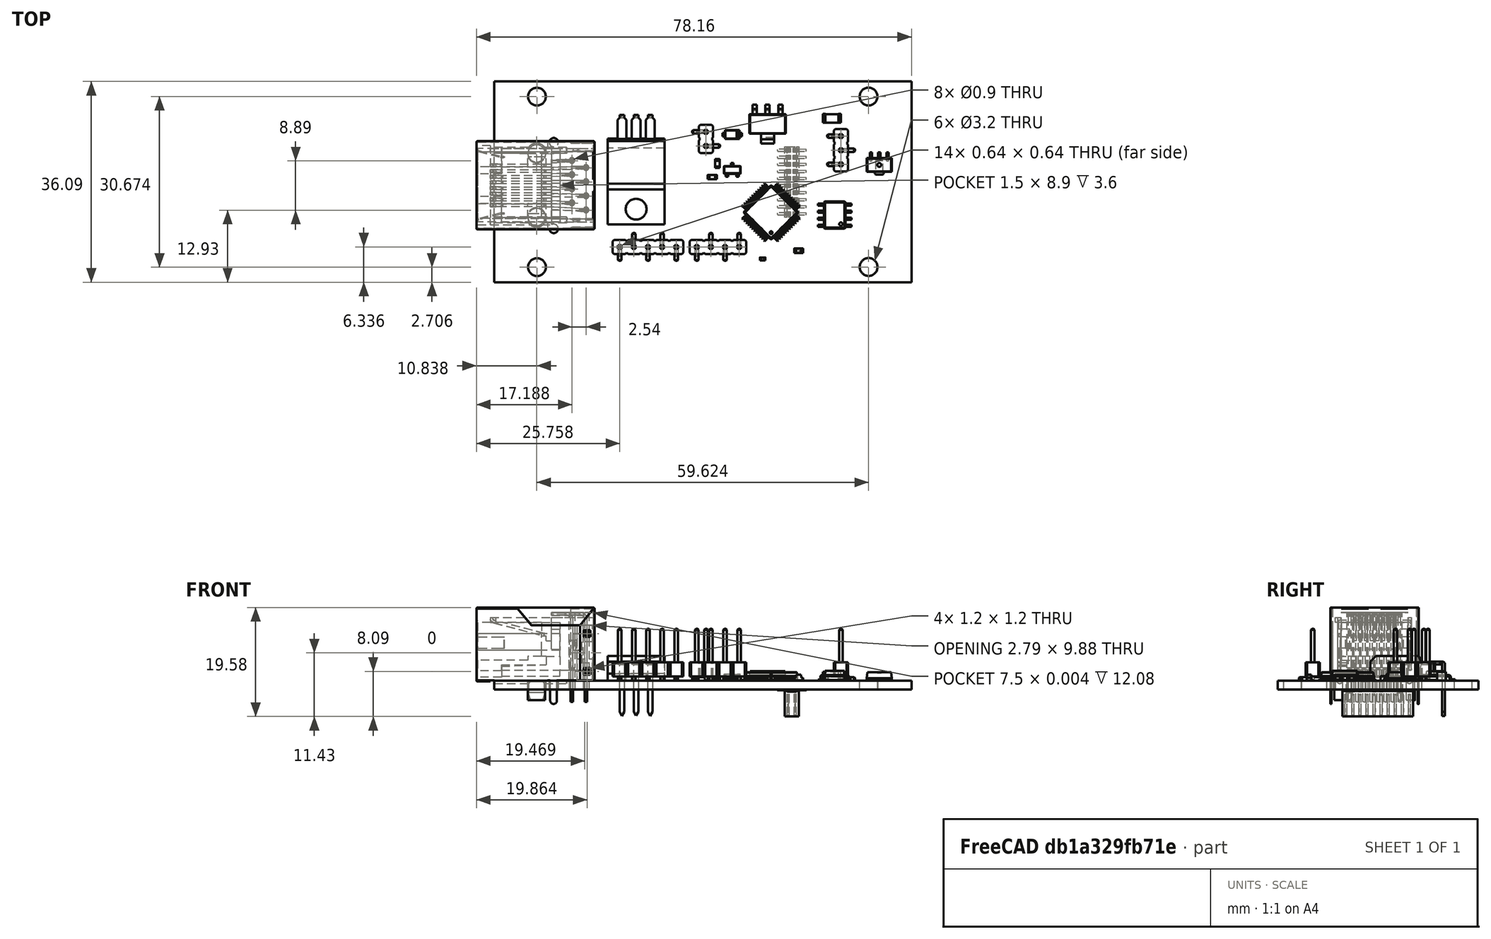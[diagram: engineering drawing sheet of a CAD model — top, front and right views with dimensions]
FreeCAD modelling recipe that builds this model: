
FCSTD DOCUMENT  (FreeCAD 0.19R24276 (Git))
Label: controle
License: Creative Commons Attribution-NonCommercial-ShareAlike
LicenseURL: http://creativecommons.org/licenses/by-nc-sa/4.0/
objects: App::Link×24, Part::Feature×19, App::LinkGroup×8, PartDesign::Line×4, PartDesign::CoordinateSystem×2, Sketcher::SketchObject×1, App::Part×1
note: 26 computed .brp shape members not serialized (recipe doc carries the construction recipe); baked Part::Feature solids carry a one-line shape summary decoded from their .brp

FEATURE [PartDesign::CoordinateSystem] Local_CS_266e
  AttacherType = Attacher::AttachEngine3D
FEATURE [Part::Feature] Pcb_266e
  Placement = pos=(-125.663,89.27,0) rot=(0,0,1;0rad)
  shape: bbox 75 x 36.09 x 1.6 mm, 22 faces (baked)
FEATURE [Sketcher::SketchObject] PCB_Sketch_266e
  FullyConstrained = false
  sketch-geometry (4):
    g0: LineSegment StartX=70.0635 StartY=0.77064 StartZ=0 EndX=-4.94 EndY=0.77 EndZ=0
    g1: LineSegment StartX=70.0635 StartY=36.856 StartZ=0 EndX=70.0635 EndY=0.77064 EndZ=0
    g2: LineSegment StartX=-4.94 StartY=36.856 StartZ=0 EndX=70.0635 EndY=36.856 EndZ=0
    g3: LineSegment StartX=-4.94 StartY=0.77 StartZ=0 EndX=-4.94 EndY=36.856 EndZ=0
  constraints (4):
    c: Coincident(g0,g3)
    c: Coincident(g2,g3)
    c: Coincident(g0,g1)
    c: Coincident(g1,g2)
FEATURE [App::LinkGroup] Board_Geoms_266e
  ElementList = -> [Pcb_266e,Local_CS_266e,PCB_Sketch_266e]
  LinkMode = 0
FEATURE [App::LinkGroup] TopV_266e
  LinkMode = 0
FEATURE [App::LinkGroup] BotV_266e
  LinkMode = 0
FEATURE [App::LinkGroup] Step_Virtual_Models_266e
  ElementList = -> [TopV_266e,BotV_266e]
  LinkMode = 0
FEATURE [Part::Feature] Shape  label="R103_R_0603_1608Metric_607532D5"
  Placement = pos=(35.1841,22.092,0) rot=(0,0,-1;1.5708rad)
  shape: bbox 0.8 x 1.6 x 0.45 mm, 26 faces (baked)
FEATURE [Part::Feature] Shape001  label="J103_PinHeader_1x02_P254mm_Vertical_SMD_Pin1Left_60752E1C"
  Placement = pos=(33.1521,26.537,0) rot=(0,0,1;0rad)
  shape: bbox 5 x 5.08 x 9.3 mm, 58 faces (baked)
FEATURE [App::Link] R103_R_0603_1608Metric_607532D5_ln_  label="R102_R_0603_1608Metric_60753017"
  LinkPlacement = pos=(38.8671,17.266,0) rot=(0,0,1;3.14159rad)
  LinkedObject = -> Shape
  Placement = pos=(38.8671,17.266,0) rot=(0,0,1;3.14159rad)
FEATURE [App::Link] R103_R_0603_1608Metric_607532D5_ln_001  label="R101_R_0603_1608Metric_60753692"
  LinkPlacement = pos=(37.9781,24.505,0) rot=(0,0,1;3.14159rad)
  LinkedObject = -> Shape
  Placement = pos=(37.9781,24.505,0) rot=(0,0,1;3.14159rad)
FEATURE [Part::Feature] Shape002  label="Q101_SOT_23_6075318C"
  Placement = pos=(37.8511,20.949,0) rot=(0,0,1;1.5708rad)
  shape: bbox 3 x 2.5 x 1.2 mm, 76 faces (baked)
FEATURE [Part::Feature] Shape003  label="C104_C_1206_3216Metric_60753A85"
  Placement = pos=(55.7581,30.22,0) rot=(0,0,1;3.14159rad)
  shape: bbox 3.2 x 1.6 x 1.6 mm, 28 faces (baked)
FEATURE [App::Link] C104_C_1206_3216Metric_60753A85_ln_  label="C103_C_1206_3216Metric_60752CED"
  LinkPlacement = pos=(40.8991,21.838,0) rot=(0,0,1;1.5708rad)
  LinkedObject = -> Shape003
  Placement = pos=(40.8991,21.838,0) rot=(0,0,1;1.5708rad)
FEATURE [App::Link] C104_C_1206_3216Metric_60753A85_ln_001  label="C102_C_1206_3216Metric_60752EF7"
  LinkPlacement = pos=(43.3121,21.838,0) rot=(0,0,1;1.5708rad)
  LinkedObject = -> Shape003
  Placement = pos=(43.3121,21.838,0) rot=(0,0,1;1.5708rad)
FEATURE [App::Link] C104_C_1206_3216Metric_60753A85_ln_002  label="C12_C_1206_3216Metric_60752D4D"
  LinkPlacement = pos=(57.7393,7.25838,0) rot=(0,0,1;3.14159rad)
  LinkedObject = -> Shape003
  Placement = pos=(57.7393,7.25838,0) rot=(0,0,1;3.14159rad)
FEATURE [App::Link] C104_C_1206_3216Metric_60753A85_ln_003  label="C7_C_1206_3216Metric_60752DAD"
  LinkPlacement = pos=(45.8521,21.711,0) rot=(0,0,-1;1.5708rad)
  LinkedObject = -> Shape003
  Placement = pos=(45.8521,21.711,0) rot=(0,0,-1;1.5708rad)
FEATURE [App::Link] C104_C_1206_3216Metric_60753A85_ln_004  label="C6_C_1206_3216Metric_60752E64"
  LinkPlacement = pos=(27.6911,26.41,0) rot=(0,0,-1;1.5708rad)
  LinkedObject = -> Shape003
  Placement = pos=(27.6911,26.41,0) rot=(0,0,-1;1.5708rad)
FEATURE [App::Link] C104_C_1206_3216Metric_60753A85_ln_005  label="C5_C_1206_3216Metric_60752F27"
  LinkPlacement = pos=(27.6911,31.617,0) rot=(0,0,1;1.5708rad)
  LinkedObject = -> Shape003
  Placement = pos=(27.6911,31.617,0) rot=(0,0,1;1.5708rad)
FEATURE [App::Link] C104_C_1206_3216Metric_60753A85_ln_006  label="C4_C_1206_3216Metric_60753077"
  LinkPlacement = pos=(37.8511,29.839,0) rot=(0,0,1;3.14159rad)
  LinkedObject = -> Shape003
  Placement = pos=(37.8511,29.839,0) rot=(0,0,1;3.14159rad)
FEATURE [App::Link] C104_C_1206_3216Metric_60753A85_ln_007  label="C3_C_1206_3216Metric_60752E94"
  LinkPlacement = pos=(50.4241,30.22,0) rot=(0,0,1;3.14159rad)
  LinkedObject = -> Shape003
  Placement = pos=(50.4241,30.22,0) rot=(0,0,1;3.14159rad)
FEATURE [App::Link] C104_C_1206_3216Metric_60753A85_ln_008  label="C2_C_1206_3216Metric_60753755"
  LinkPlacement = pos=(64.7751,26.029,0) rot=(0,0,1;3.14159rad)
  LinkedObject = -> Shape003
  Placement = pos=(64.7751,26.029,0) rot=(0,0,1;3.14159rad)
FEATURE [App::Link] C104_C_1206_3216Metric_60753A85_ln_009  label="C1_C_1206_3216Metric_60752D7D"
  LinkPlacement = pos=(55.7581,32.76,0) rot=(0,0,1;3.14159rad)
  LinkedObject = -> Shape003
  Placement = pos=(55.7581,32.76,0) rot=(0,0,1;3.14159rad)
FEATURE [Part::Feature] Shape004  label="U401_SOT_89_3_607525BD"
  Placement = pos=(64.2671,22.092,0) rot=(0,0,-1;1.5708rad)
  shape: bbox 4.5 x 4 x 1.52 mm, 43 faces (baked)
FEATURE [Part::Feature] Shape005  label="J102_PinHeader_1x05_P254mm_Vertical_SMD_Pin1Left_607527F2"
  Placement = pos=(22.7381,7.10598,0) rot=(0,0,1;1.5708rad)
  shape: bbox 12.7 x 5 x 9.3 mm, 139 faces (baked)
FEATURE [Part::Feature] Shape006  label="D102_D_SOD_123F_60752671"
  Placement = pos=(37.8511,27.299,0) rot=(0,0,1;3.14159rad)
  shape: bbox 3.5 x 1.6 x 1.1 mm, 27 faces (baked)
FEATURE [Part::Feature] Shape007  label="U601_SOIC_8_39x49mm_P127mm_6075390B"
  Placement = pos=(56.2661,12.821,0) rot=(0,0,1;3.14159rad)
  shape: bbox 6 x 4.9 x 1.75 mm, 156 faces (baked)
FEATURE [Part::Feature] Shape008  label="D501_LED_0603_1608Metric_6077B07B"
  Placement = pos=(49.7841,6.40898,0) rot=(0,0,1;3.14159rad)
  shape: bbox 1.6 x 0.8 x 1.1 mm, 50 faces (baked)
FEATURE [App::Link] R103_R_0603_1608Metric_607532D5_ln_002  label="R502_R_0603_1608Metric_6077B043"
  LinkPlacement = pos=(49.7841,7.91878,0) rot=(0,0,1;0rad)
  LinkedObject = -> Shape
  Placement = pos=(49.7841,7.91878,0) rot=(0,0,1;0rad)
FEATURE [Part::Feature] Shape009  label="U501_LQFP_48_7x7mm_P05mm_607528ED"
  Placement = pos=(44.8361,13.329,0) rot=(0,0,1;2.35619rad)
  shape: bbox 10.41 x 10.41 x 1.5 mm, 764 faces (baked)
FEATURE [App::Link] R103_R_0603_1608Metric_607532D5_ln_003  label="R505_R_0603_1608Metric_60752576"
  LinkPlacement = pos=(41.5341,6.08998,0) rot=(0,0,1;1.5708rad)
  LinkedObject = -> Shape
  Placement = pos=(41.5341,6.08998,0) rot=(0,0,1;1.5708rad)
FEATURE [Part::Feature] Shape010  label="R504_R_0402_1005Metric_6075253D"
  Placement = pos=(43.3121,4.94698,0) rot=(0,0,1;3.14159rad)
  shape: bbox 1 x 0.5 x 0.35 mm, 26 faces (baked)
FEATURE [Part::Feature] Shape011  label="J101_PinHeader_1x04_P254mm_Vertical_SMD_Pin1Left_60752A18"
  Placement = pos=(35.3111,7.10598,0) rot=(0,0,1;1.5708rad)
  shape: bbox 10.16 x 5 x 9.3 mm, 112 faces (baked)
FEATURE [Part::Feature] Shape012  label="C201_C_0603_1608Metric_6075323F"
  Placement = pos=(34.2686,19.674,0) rot=(0,0,1;0rad)
  shape: bbox 1.6 x 0.8 x 0.8 mm, 28 faces (baked)
FEATURE [App::Link] R103_R_0603_1608Metric_607532D5_ln_004  label="R205_R_0603_1608Metric_60752B49"
  LinkPlacement = pos=(28.8341,22.854,0) rot=(0,0,1;0rad)
  LinkedObject = -> Shape
  Placement = pos=(28.8341,22.854,0) rot=(0,0,1;0rad)
FEATURE [App::Link] R103_R_0603_1608Metric_607532D5_ln_005  label="R204_R_0603_1608Metric_60752A9B"
  LinkPlacement = pos=(31.5011,20.314,0) rot=(0,0,-1;1.5708rad)
  LinkedObject = -> Shape
  Placement = pos=(31.5011,20.314,0) rot=(0,0,-1;1.5708rad)
FEATURE [App::Link] R103_R_0603_1608Metric_607532D5_ln_006  label="R203_R_0603_1608Metric_60752C51"
  LinkPlacement = pos=(29.8501,20.314,0) rot=(0,0,-1;1.5708rad)
  LinkedObject = -> Shape
  Placement = pos=(29.8501,20.314,0) rot=(0,0,-1;1.5708rad)
FEATURE [App::Link] C201_C_0603_1608Metric_6075323F_ln_  label="C202_C_0603_1608Metric_607526B4"
  LinkPlacement = pos=(32.3901,22.854,0) rot=(0,0,1;0rad)
  LinkedObject = -> Shape012
  Placement = pos=(32.3901,22.854,0) rot=(0,0,1;0rad)
FEATURE [Part::Feature] Shape013  label="U403_TO-220-3_Horizontal_TabDown_607524A3"
  Placement = pos=(23.1191,30.601,0) rot=(0,0,1;3.14159rad)
  shape: bbox 10.25 x 19.74 x 10.78 mm, 80 faces (baked)
FEATURE [Part::Feature] Shape014  label="U402_SOT_223_6075262C"
  Placement = pos=(44.2011,29.204,0) rot=(0,0,-1;1.5708rad)
  shape: bbox 6.5 x 7 x 1.7 mm, 78 faces (baked)
FEATURE [App::Link] D102_D_SOD_123F_60752671_ln_  label="D101_D_SOD_123F_6075328F"
  LinkPlacement = pos=(10.4191,31.998,0) rot=(0,0,1;3.14159rad)
  LinkedObject = -> Shape006
  Placement = pos=(10.4191,31.998,0) rot=(0,0,1;3.14159rad)
FEATURE [App::Link] C201_C_0603_1608Metric_6075323F_ln_001  label="C11_C_0603_1608Metric_60753953"
  LinkPlacement = pos=(47.2491,5.96298,0) rot=(0,0,1;1.5708rad)
  LinkedObject = -> Shape012
  Placement = pos=(47.2491,5.96298,0) rot=(0,0,1;1.5708rad)
FEATURE [App::Link] C201_C_0603_1608Metric_6075323F_ln_002  label="C9_C_0603_1608Metric_60752F87"
  LinkPlacement = pos=(48.7731,19.806,0) rot=(0,0,1;3.14159rad)
  LinkedObject = -> Shape012
  Placement = pos=(48.7731,19.806,0) rot=(0,0,1;3.14159rad)
FEATURE [App::Link] C201_C_0603_1608Metric_6075323F_ln_003  label="C10_C_0603_1608Metric_6075386F"
  LinkPlacement = pos=(38.1051,13.329,0) rot=(0,0,-1;1.5708rad)
  LinkedObject = -> Shape012
  Placement = pos=(38.1051,13.329,0) rot=(0,0,-1;1.5708rad)
FEATURE [Part::Feature] Shape015  label="J107_PinSocket_2x10_P127mm_Vertical_SMD_606F5D48"
  Placement = pos=(48.5634,18.7697,-1.6) rot=(0,1,0;3.14159rad)
  shape: bbox 5.185 x 12.7 x 4.825 mm, 710 faces (baked)
FEATURE [App::LinkGroup] Bot_266e
  ElementList = -> [Shape015]
  LinkMode = 0
FEATURE [Part::Feature] Shape016  label="J106_PinHeader_1x03_P254mm_Vertical_SMD_Pin1Left_607539D0"
  Placement = pos=(57.4091,24.505,0) rot=(0,0,1;0rad)
  shape: bbox 5 x 7.62 x 9.3 mm, 85 faces (baked)
FEATURE [App::Link] J106_PinHeader_1x03_P254mm_Vertical_SMD_Pin1Left_607539D0_ln_  label="J105_PinHeader_1x03_P254mm_Vertical_SMD_Pin1Left_60753A33"
  LinkPlacement = pos=(51.4401,24.505,0) rot=(0,0,1;0rad)
  LinkedObject = -> Shape016
  Placement = pos=(51.4401,24.505,0) rot=(0,0,1;0rad)
FEATURE [App::Link] C201_C_0603_1608Metric_6075323F_ln_004  label="C8_C_0603_1608Metric_60753047"
  LinkPlacement = pos=(44.0741,6.34398,0) rot=(0,0,1;0rad)
  LinkedObject = -> Shape012
  Placement = pos=(44.0741,6.34398,0) rot=(0,0,1;0rad)
FEATURE [Part::Feature] _15008142621_1_fd_cp  label="615008142621_1_sp"
  Placement = pos=(2.5,18.2,6.5) rot=(0,0,-1;1.5708rad)
  shape: bbox 21.2 x 15.88 x 17.34 mm, 703 faces (baked)
FEATURE [App::LinkGroup] Top_266e
  ElementList = -> [Shape,Shape001,R103_R_0603_1608Metric_607532D5_ln_,R103_R_0603_1608Metric_607532D5_ln_001,Shape002,Shape003,C104_C_1206_3216Metric_60753A85_ln_,C104_C_1206_3216Metric_60753A85_ln_001,C104_C_1206_3216Metric_60753A85_ln_002,C104_C_1206_3216Metric_60753A85_ln_003,C104_C_1206_3216Metric_60753A85_ln_004,C104_C_1206_3216Metric_60753A85_ln_005,C104_C_1206_3216Metric_60753A85_ln_006,+28 more]
  LinkMode = 0
FEATURE [App::LinkGroup] Step_Models_266e
  ElementList = -> [Top_266e,Bot_266e]
  LinkMode = 0
FEATURE [App::LinkGroup] Board_266e  label="Controle"
  ElementList = -> [Board_Geoms_266e,Step_Models_266e,Step_Virtual_Models_266e]
  LinkMode = 0
FEATURE [PartDesign::CoordinateSystem] LCS_0
  AttacherType = Attacher::AttachEngine3D
  MapMode = 2
  Support = -> [X_Axis]
FEATURE [PartDesign::Line] HoleAxis_1
  AttacherType = Attacher::AttachEngineLine
  Length = 4.50902
  MapMode = 19
  Placement = pos=(62.35,34.15,0) rot=(0,0,1;0rad)
  ResizeMode = 1
  Support = -> [Pcb_266e]
FEATURE [PartDesign::Line] HoleAxis_2
  AttacherType = Attacher::AttachEngineLine
  Length = 4.50902
  MapMode = 19
  Placement = pos=(2.7604,34.1266,0) rot=(0,0,1;0rad)
  ResizeMode = 1
  Support = -> [Pcb_266e]
FEATURE [PartDesign::Line] HoleAxis_3
  AttacherType = Attacher::AttachEngineLine
  Length = 4.50902
  MapMode = 19
  Placement = pos=(2.77348,3.47598,0) rot=(0,0,1;0rad)
  ResizeMode = 1
  Support = -> [Pcb_266e]
FEATURE [PartDesign::Line] HoleAxis_4
  AttacherType = Attacher::AttachEngineLine
  Length = 4.50902
  MapMode = 19
  Placement = pos=(62.3621,3.5,0) rot=(0,0,1;0rad)
  ResizeMode = 1
  Support = -> [Pcb_266e]
FEATURE [App::Part] Part
  Group = -> [LCS_0,R103_R_0603_1608Metric_607532D5_ln_001,TopV_266e,Shape,Shape002,C104_C_1206_3216Metric_60753A85_ln_001,C104_C_1206_3216Metric_60753A85_ln_,C104_C_1206_3216Metric_60753A85_ln_003,C104_C_1206_3216Metric_60753A85_ln_004,C104_C_1206_3216Metric_60753A85_ln_005,C104_C_1206_3216Metric_60753A85_ln_006,C104_C_1206_3216Metric_60753A85_ln_007,Shape004,C104_C_1206_3216Metric_60753A85_ln_002,Shape003,+43 more]
  Origin = -> Origin
